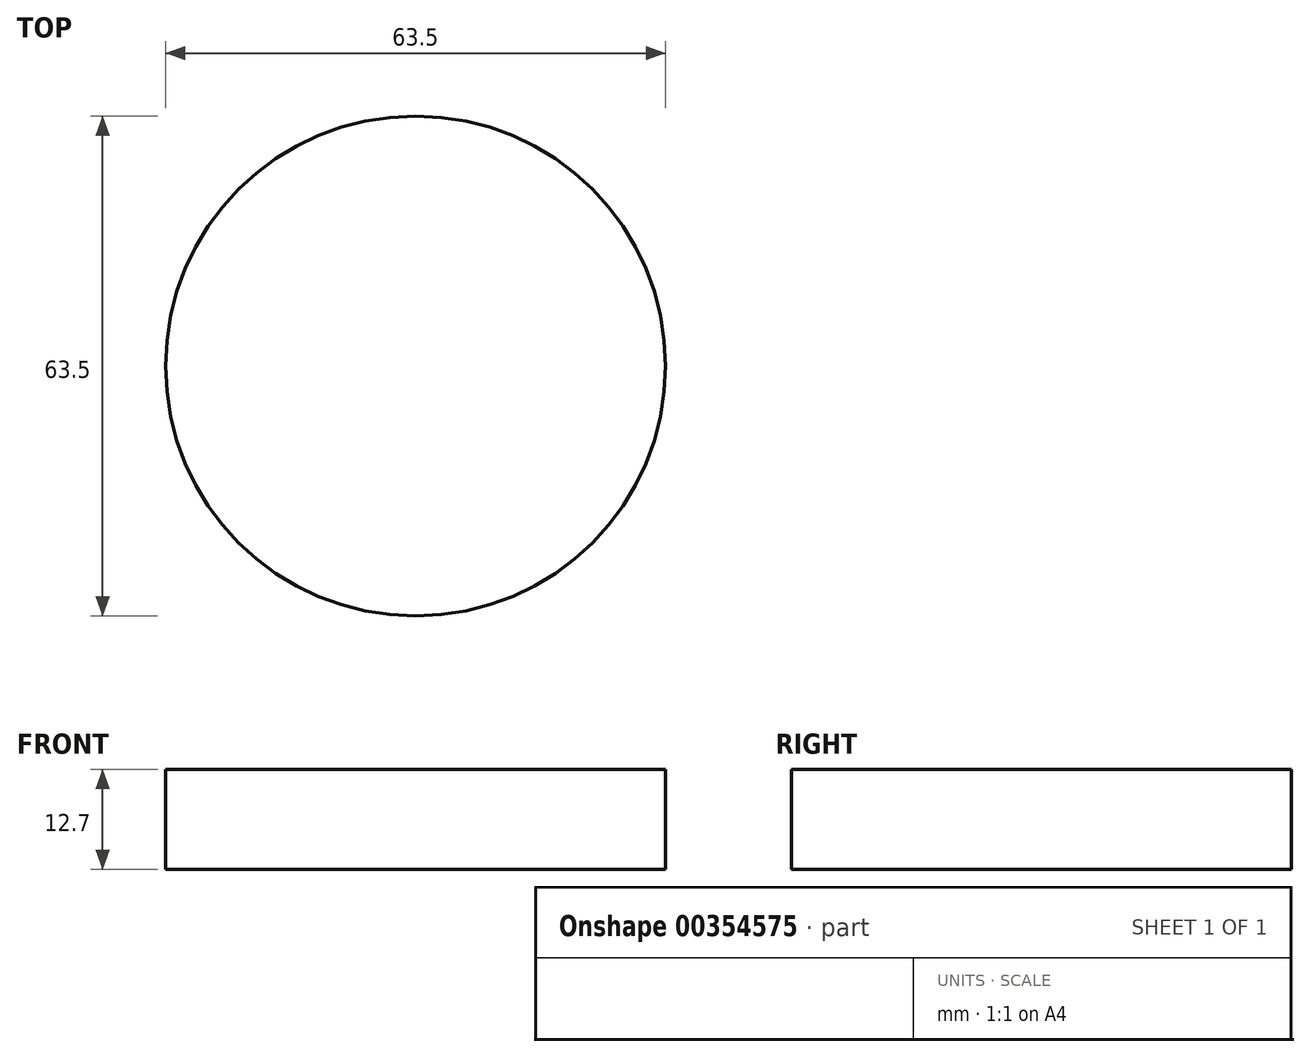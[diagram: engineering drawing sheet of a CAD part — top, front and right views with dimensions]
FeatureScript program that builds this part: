
annotation { "Feature Type Name" : "Feature", "Feature Type Description" : "" }
export const myFeature = defineFeature(function(context is Context, id is Id, definition is map)
    precondition{}
    {
        {
            var Q0;
            Q0=qCreatedBy(makeId("Top.planeOp"),FACE);
            var sketch = newSketch(context, id + "F0", { "sketchPlane" : qUnion([Q0])});
            skCircle(sketch, "E0", {"center": v(0, 0) * mm, "radius": 31.75 * mm});
            skSolve(sketch);
        }
        {
            var Q0;
            Q0 = qSketchRegion(id + "F0", true);
            extrude(context, id + "F1", {"entities" : qUnion([Q0]), "depth" : 12.7 * mm});
        }
    });
